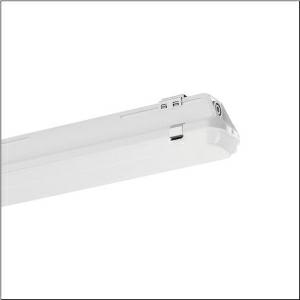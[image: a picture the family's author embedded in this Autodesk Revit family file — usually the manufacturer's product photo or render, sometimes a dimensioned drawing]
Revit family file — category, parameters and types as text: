
# Revit family: monsun_r__12_51fp208p430h_b7ff
name_source: partatom
category: Lighting Fixtures
units: mm (PartAtom-declared; Revit-internal decimal feet)

## family parameters
Cut with Voids When Loaded = No
Host = Face
Light Source = No
Part Type = Normal
Room Calculation Point = No
Round Connector Dimension = Use Diameter
Shared = No

## types (1)
- Monsun® 12 (1 x LED, 3990 lm, 24.8 W, 4000K)
    Apparent Load = 25 VA
    CIE Flux Codes = 45 75 93 94 100
    Color Rendering = 80
    Color Temperature = 4000K
    Default Elevation = 1800 mm
    Description = Monsun® 12, damp-proof luminaire, chain hanger, primary optical cover: enclosure, of PC, light emission: direct distribution, primary light characteristic: symmetric, installation type: suspended mounting, surface-mounted, horizontal mounting, vertical mounting, LED rated luminous flux: 3.990 lm, light colour: 840, colour temperature: 4000K, control gear: ECG, with terminal, 3-pole, max. 2.5mm², mains connection: 220..240V, AC, 50/60Hz, rated input power: 25W, luminaire housing, of glass-fibre reinforced polyester, uncoated, bright grey, length: 1.590 mm, width: 90 mm, height: 88mm, clip for enclosure, of stainless steel (V2A), ceiling mounting element, of stainless steel (V2A), chain hanger, of stainless steel (V2A), protection rating (complete): IP66, insulation class (complete): insulation class I (protective earthing), certification: CE, ENEC, VDE, protection symbol: D, impact resistance: IK08, permissible ambient temperature for indoor applications: -35..+40°C, standard: EN 50419, EN 60598-2-1, no direct snow, no direct sun, no direct rain, for indoor or canopied outdoor use, corresponds to IFS (International Featured Standards) requirements for safety and quality in the food industry, packaging unit: 1 piece
    Height = 89 mm
    Lamp = 1 x LED
    Lamp Light Flux = 3990 lm
    Lamp Power = 24.8 W
    Lamp count = 1
    Length = 1590 mm
    Luminous efficacy = 161 lm/W
    Manufacturer = Siteco
    ModVariant = No
    Model = 51FP208P430H
    Mounting Place = Ceiling
    Mounting Type = Pendant
    Number of Poles = 1
    OnlyDefault = Yes
    Power Factor = 1
    Product Name = Monsun® 12
    Product group = damp-proof luminaire | ceiling pendant
    ProductGroupID = 908
    Protection Class = Protection class I
    Protection Degree = IP 66
    RLX_Detail_Level = 1
    RlxData = <blob elided: 88569 chars, md5=39c7c1e9>
    Socket = socket
    Standby Power = 0 W
    System Light Flux = 3990 lm
    System Power = 25 W
    Type Comments = Product without accessories
    Type Image = l_1004748.jpg
    URL = http://relux.com
    VarID = ---
    Voltage = 0 V
    Weight = 0.00 kg
    Width = 90 mm

## geometry (parser evidence)
native form markers: Blend x4, Sweep x14
no freeform markers — native parametric forms only
